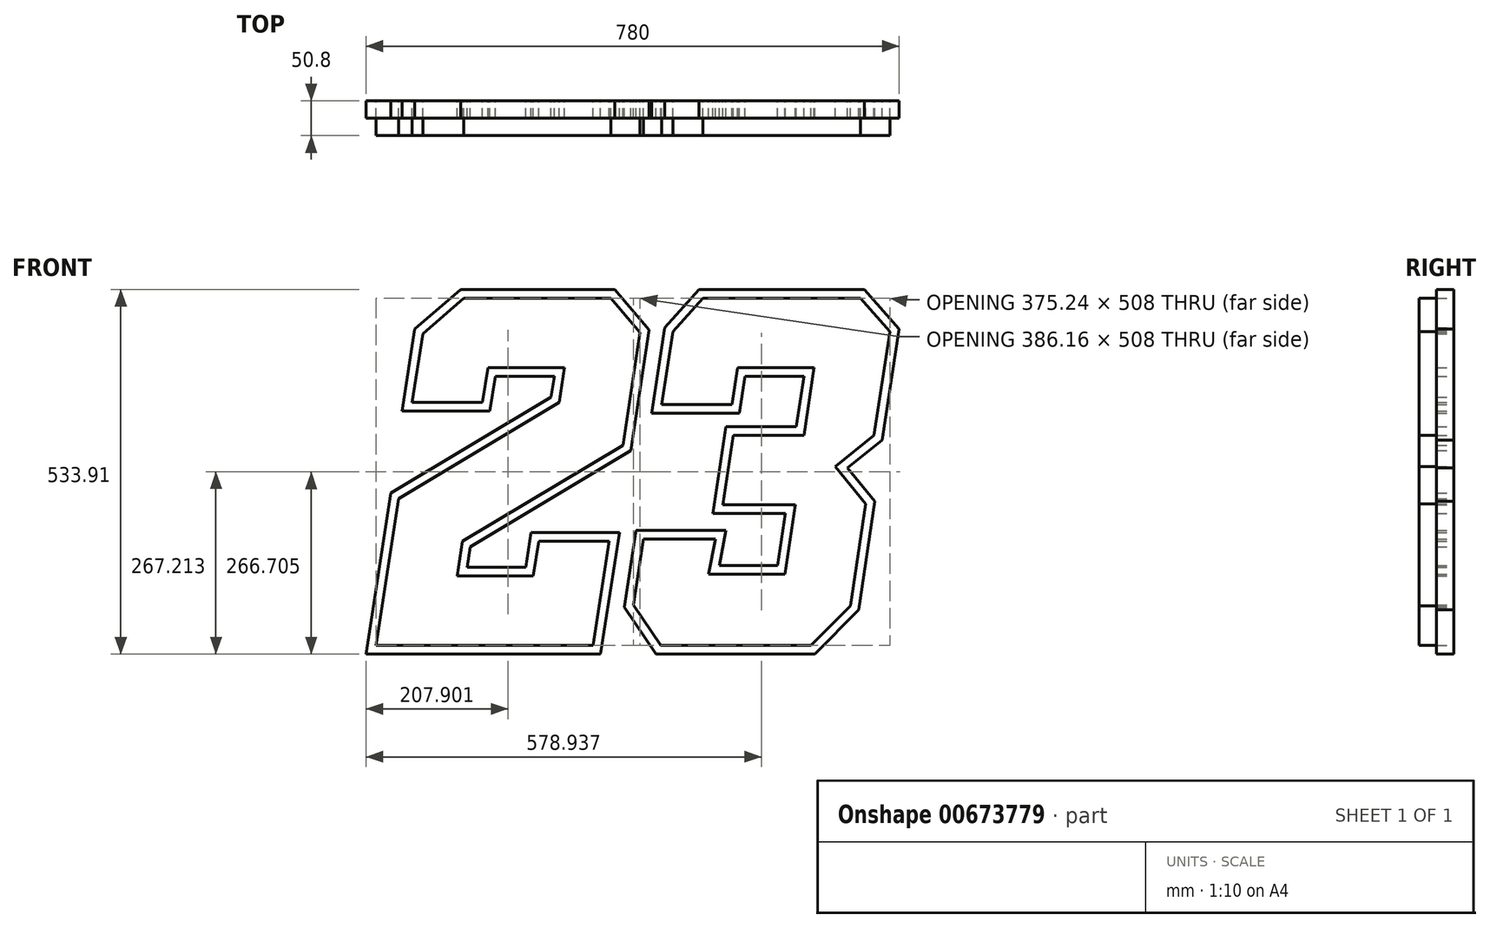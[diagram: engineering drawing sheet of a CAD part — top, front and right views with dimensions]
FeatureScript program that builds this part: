
annotation { "Feature Type Name" : "Feature", "Feature Type Description" : "" }
export const myFeature = defineFeature(function(context is Context, id is Id, definition is map)
    precondition{}
    {
        {
            var Q0;
            Q0=qCreatedBy(makeId("Front.planeOp"),FACE);
            var sketch = newSketch(context, id + "F0", { "sketchPlane" : qUnion([Q0])});
            skLineSegment(sketch, "E0.top", {"start": v(-53.99, 119.08) * mm, "end": v(263.51, 119.08) * mm});
            skLineSegment(sketch, "E1", {"start": v(-0.95, 474.68) * mm, "end": v(14.67, 575.48) * mm});
            skLineSegment(sketch, "E2", {"start": v(14.67, 575.48) * mm, "end": v(74.38, 627.08) * mm});
            skLineSegment(sketch, "E3", {"start": v(74.38, 627.08) * mm, "end": v(289.46, 627.08) * mm});
            skLineSegment(sketch, "E4", {"start": v(289.46, 627.08) * mm, "end": v(332.17, 577.37) * mm});
            skLineSegment(sketch, "E5", {"start": v(332.17, 577.37) * mm, "end": v(307.1, 412.14) * mm});
            skLineSegment(sketch, "E6", {"start": v(307.1, 412.14) * mm, "end": v(72.45, 271.48) * mm});
            skLineSegment(sketch, "E7", {"start": v(72.45, 271.48) * mm, "end": v(64.57, 220.68) * mm});
            skLineSegment(sketch, "E8", {"start": v(64.57, 220.68) * mm, "end": v(176.28, 220.68) * mm});
            skLineSegment(sketch, "E9", {"start": v(176.28, 220.68) * mm, "end": v(183.98, 271.48) * mm});
            skLineSegment(sketch, "E10", {"start": v(183.98, 271.48) * mm, "end": v(287.18, 271.48) * mm});
            skLineSegment(sketch, "E11", {"start": v(287.18, 271.48) * mm, "end": v(263.51, 119.08) * mm});
            skLineSegment(sketch, "E12", {"start": v(-53.99, 119.08) * mm, "end": v(-20.66, 334.13) * mm});
            skLineSegment(sketch, "E13", {"start": v(-20.66, 334.13) * mm, "end": v(213.83, 474.68) * mm});
            skLineSegment(sketch, "E14", {"start": v(213.83, 474.68) * mm, "end": v(221.53, 525.48) * mm});
            skLineSegment(sketch, "E15", {"start": v(221.53, 525.48) * mm, "end": v(109.73, 525.48) * mm});
            skLineSegment(sketch, "E16", {"start": v(109.73, 525.48) * mm, "end": v(101.86, 474.68) * mm});
            skLineSegment(sketch, "E17", {"start": v(101.86, 474.68) * mm, "end": v(-0.95, 474.68) * mm});
            skLineSegment(sketch, "E18", {"start": v(380.25, 578.31) * mm, "end": v(424.5, 627.6) * mm});
            skLineSegment(sketch, "E19", {"start": v(424.5, 627.6) * mm, "end": v(654.58, 627.6) * mm});
            skLineSegment(sketch, "E20", {"start": v(654.58, 627.6) * mm, "end": v(697.75, 578.4) * mm});
            skLineSegment(sketch, "E21", {"start": v(697.75, 578.4) * mm, "end": v(674.73, 426.73) * mm});
            skLineSegment(sketch, "E22", {"start": v(674.73, 426.73) * mm, "end": v(618.05, 380.9) * mm});
            skLineSegment(sketch, "E23", {"start": v(618.05, 380.9) * mm, "end": v(662.61, 326.28) * mm});
            skLineSegment(sketch, "E24", {"start": v(662.61, 326.28) * mm, "end": v(640, 177.3) * mm});
            skLineSegment(sketch, "E25", {"start": v(640, 177.3) * mm, "end": v(582.66, 119.6) * mm});
            skLineSegment(sketch, "E26", {"start": v(582.66, 119.6) * mm, "end": v(362.65, 119.6) * mm});
            skLineSegment(sketch, "E27", {"start": v(362.65, 119.6) * mm, "end": v(322.5, 178.45) * mm});
            skLineSegment(sketch, "E28", {"start": v(322.5, 178.45) * mm, "end": v(337.13, 274.8) * mm});
            skLineSegment(sketch, "E29", {"start": v(337.13, 274.8) * mm, "end": v(442.73, 274.8) * mm});
            skLineSegment(sketch, "E30", {"start": v(442.73, 274.8) * mm, "end": v(432.8, 223.67) * mm});
            skLineSegment(sketch, "E31", {"start": v(432.8, 223.67) * mm, "end": v(544.28, 223.67) * mm});
            skLineSegment(sketch, "E32", {"start": v(544.28, 223.67) * mm, "end": v(559.7, 325.27) * mm});
            skLineSegment(sketch, "E33", {"start": v(559.7, 325.27) * mm, "end": v(453.6, 325.27) * mm});
            skLineSegment(sketch, "E34", {"start": v(453.6, 325.27) * mm, "end": v(469, 426.87) * mm});
            skLineSegment(sketch, "E35", {"start": v(469, 426.87) * mm, "end": v(572, 426.87) * mm});
            skLineSegment(sketch, "E36", {"start": v(572, 426.87) * mm, "end": v(587.03, 526) * mm});
            skLineSegment(sketch, "E37", {"start": v(587.03, 526) * mm, "end": v(475.07, 526) * mm});
            skLineSegment(sketch, "E38", {"start": v(475.07, 526) * mm, "end": v(466.86, 471.9) * mm});
            skLineSegment(sketch, "E39", {"start": v(466.86, 471.9) * mm, "end": v(364.1, 471.9) * mm});
            skLineSegment(sketch, "E40", {"start": v(364.1, 471.9) * mm, "end": v(380.25, 578.31) * mm});
            skLineSegment(sketch, "E41.0", {"start": v(120.62, 512.78) * mm, "end": v(112.74, 461.98) * mm});
            skLineSegment(sketch, "E41.1", {"start": v(206.76, 512.78) * mm, "end": v(120.62, 512.78) * mm});
            skLineSegment(sketch, "E41.2", {"start": v(202.17, 482.5) * mm, "end": v(206.76, 512.78) * mm});
            skLineSegment(sketch, "E41.3", {"start": v(-32.3, 341.96) * mm, "end": v(202.17, 482.5) * mm});
            skLineSegment(sketch, "E41.4", {"start": v(-68.8, 106.38) * mm, "end": v(-32.3, 341.96) * mm});
            skLineSegment(sketch, "E41.5", {"start": v(112.74, 461.98) * mm, "end": v(-15.77, 461.98) * mm});
            skLineSegment(sketch, "E41.6", {"start": v(-68.8, 106.38) * mm, "end": v(274.4, 106.38) * mm});
            skLineSegment(sketch, "E41.7", {"start": v(302, 284.18) * mm, "end": v(274.4, 106.38) * mm});
            skLineSegment(sketch, "E41.8", {"start": v(295.3, 639.78) * mm, "end": v(345.6, 581.22) * mm});
            skLineSegment(sketch, "E41.9", {"start": v(69.65, 639.78) * mm, "end": v(295.3, 639.78) * mm});
            skLineSegment(sketch, "E41.10", {"start": v(2.83, 582.03) * mm, "end": v(69.65, 639.78) * mm});
            skLineSegment(sketch, "E41.11", {"start": v(-15.77, 461.98) * mm, "end": v(2.83, 582.03) * mm});
            skLineSegment(sketch, "E41.12", {"start": v(345.6, 581.22) * mm, "end": v(318.76, 404.32) * mm});
            skLineSegment(sketch, "E41.13", {"start": v(318.76, 404.32) * mm, "end": v(84.08, 263.65) * mm});
            skLineSegment(sketch, "E41.14", {"start": v(84.08, 263.65) * mm, "end": v(79.4, 233.38) * mm});
            skLineSegment(sketch, "E41.15", {"start": v(79.4, 233.38) * mm, "end": v(165.36, 233.38) * mm});
            skLineSegment(sketch, "E41.16", {"start": v(165.36, 233.38) * mm, "end": v(173.07, 284.18) * mm});
            skLineSegment(sketch, "E41.17", {"start": v(173.07, 284.18) * mm, "end": v(302, 284.18) * mm});
            skLineSegment(sketch, "E42.0", {"start": v(309.2, 175.41) * mm, "end": v(326.2, 287.5) * mm});
            skLineSegment(sketch, "E42.1", {"start": v(355.94, 106.9) * mm, "end": v(309.2, 175.41) * mm});
            skLineSegment(sketch, "E42.2", {"start": v(587.94, 106.9) * mm, "end": v(355.94, 106.9) * mm});
            skLineSegment(sketch, "E42.3", {"start": v(651.94, 171.3) * mm, "end": v(587.94, 106.9) * mm});
            skLineSegment(sketch, "E42.4", {"start": v(676.01, 329.94) * mm, "end": v(651.94, 171.3) * mm});
            skLineSegment(sketch, "E42.5", {"start": v(635.95, 379.04) * mm, "end": v(676.01, 329.94) * mm});
            skLineSegment(sketch, "E42.6", {"start": v(418.83, 640.3) * mm, "end": v(660.33, 640.3) * mm});
            skLineSegment(sketch, "E42.7", {"start": v(660.33, 640.3) * mm, "end": v(711.19, 582.34) * mm});
            skLineSegment(sketch, "E42.8", {"start": v(711.19, 582.34) * mm, "end": v(686.55, 419.95) * mm});
            skLineSegment(sketch, "E42.9", {"start": v(686.55, 419.95) * mm, "end": v(635.95, 379.04) * mm});
            skLineSegment(sketch, "E42.10", {"start": v(368.26, 583.97) * mm, "end": v(418.83, 640.3) * mm});
            skLineSegment(sketch, "E42.11", {"start": v(326.2, 287.5) * mm, "end": v(458.13, 287.5) * mm});
            skLineSegment(sketch, "E42.12", {"start": v(458.13, 287.5) * mm, "end": v(448.2, 236.37) * mm});
            skLineSegment(sketch, "E42.13", {"start": v(448.2, 236.37) * mm, "end": v(533.36, 236.37) * mm});
            skLineSegment(sketch, "E42.14", {"start": v(533.36, 236.37) * mm, "end": v(544.92, 312.57) * mm});
            skLineSegment(sketch, "E42.15", {"start": v(544.92, 312.57) * mm, "end": v(438.82, 312.57) * mm});
            skLineSegment(sketch, "E42.16", {"start": v(438.82, 312.57) * mm, "end": v(458.09, 439.57) * mm});
            skLineSegment(sketch, "E42.17", {"start": v(458.09, 439.57) * mm, "end": v(561.07, 439.57) * mm});
            skLineSegment(sketch, "E42.18", {"start": v(561.07, 439.57) * mm, "end": v(572.26, 513.3) * mm});
            skLineSegment(sketch, "E42.19", {"start": v(572.26, 513.3) * mm, "end": v(485.99, 513.3) * mm});
            skLineSegment(sketch, "E42.20", {"start": v(485.99, 513.3) * mm, "end": v(477.78, 459.2) * mm});
            skLineSegment(sketch, "E42.21", {"start": v(477.78, 459.2) * mm, "end": v(349.33, 459.2) * mm});
            skLineSegment(sketch, "E42.22", {"start": v(349.33, 459.2) * mm, "end": v(368.26, 583.97) * mm});
            skSolve(sketch);
        }
        {
            var Q0;
            Q0 = qSketchRegion(id + "F0", true);
            extrude(context, id + "F1", {"entities" : qUnion([Q0]), "depth" : 25.4 * mm, "offsetDistance" : 25.4 * mm});
        }
        {
            var Q0;
            Q0=makeQuery(id+"F0.imprint","IMPRINT",FACE,{"disambiguationData":[TD([[makeQuery(id+"F0.imprint","IMPRINT",EDGE,{"derivedFrom":sQuery(id+"F0.wireOp",EDGE,"E18")}),-1.0]])]});
            var Q1;
            Q1=makeQuery(id+"F0.imprint","IMPRINT",FACE,{"disambiguationData":[TD([[makeQuery(id+"F0.imprint","IMPRINT",EDGE,{"derivedFrom":sQuery(id+"F0.wireOp",EDGE,"E0.top")}),1.0]])]});
            extrude(context, id + "F2", {"entities" : qUnion([Q0, Q1]), "depth" : 50.8 * mm, "offsetDistance" : 25.4 * mm});
        }
    });
